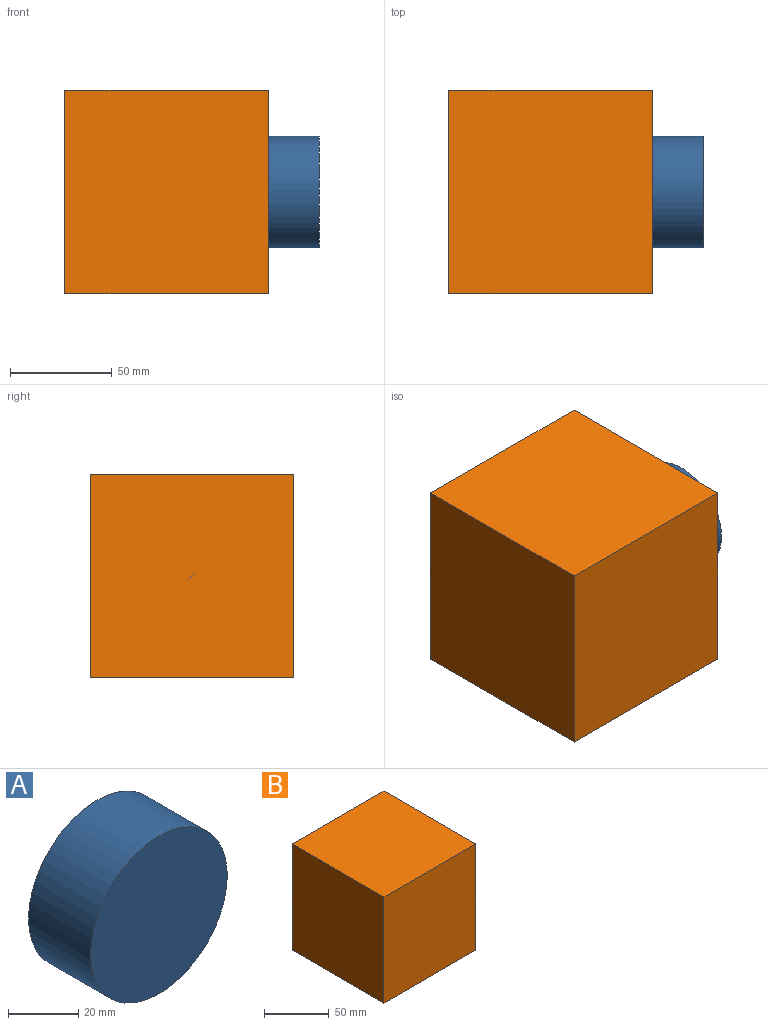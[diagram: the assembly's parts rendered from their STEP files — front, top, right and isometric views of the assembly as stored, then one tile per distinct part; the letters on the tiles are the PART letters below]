
ASSEMBLY  parts=2 mates=1
PART A: 3 faces, bbox 55.1x25x55.1 mm
  f0: cylinder r=27.53mm len=55.07mm, axis (0,1,0), area 4324.8mm2, adj f1,f2
  f1: plane 55.07x55.07mm, normal (0,-1,0), area 2381.5mm2, adj f0
  f2: plane 55.07x55.07mm, normal (0,1,0), area 2381.5mm2, adj f0
PART B: 6 faces, bbox 100x100x100 mm
  f0: plane 100x100mm, normal (-1,0,0), area 10000mm2, adj f1,f3,f4,f5
  f1: plane 100x100mm, normal (0,0,-1), area 10000mm2, adj f0,f2,f4,f5
  f2: plane 100x100mm, normal (1,0,0), area 10000mm2, adj f1,f3,f4,f5
  f3: plane 100x100mm, normal (0,0,1), area 10000mm2, adj f0,f2,f4,f5
  f4: plane 100x100mm, normal (0,-1,0), area 10000mm2, adj f0,f1,f2,f3
  f5: plane 100x100mm, normal (0,1,0), area 10000mm2, adj f0,f1,f2,f3
PLACE A rot(axis=(0.58,0.58,-0.58),120deg) t=(-68.6,-47.4,-25.77)mm
PLACE B t=(-160.16,-21.72,-10.86)mm fixed
MATE fastened A.f0 <-> B.f2  axis (-1,0,0) through (-93.6,-71.72,-12.86)mm
